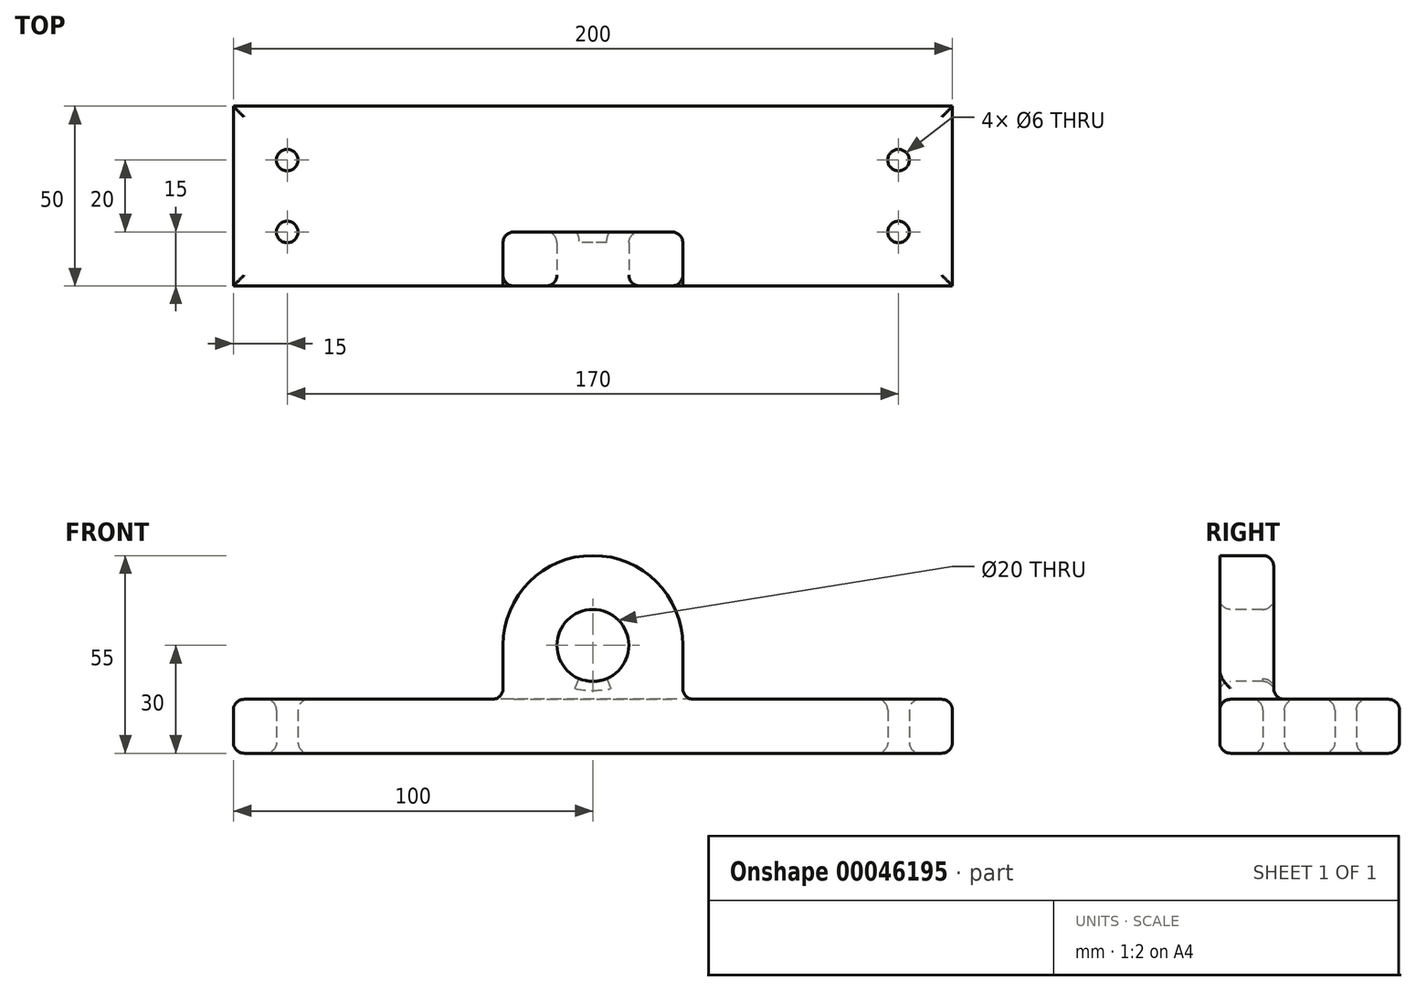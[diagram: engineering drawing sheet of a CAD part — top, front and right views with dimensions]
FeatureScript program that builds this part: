
annotation { "Feature Type Name" : "Feature", "Feature Type Description" : "" }
export const myFeature = defineFeature(function(context is Context, id is Id, definition is map)
    precondition{}
    {
        {
            var Q0;
            Q0=qCreatedBy(makeId("Top.planeOp"),FACE);
            var sketch = newSketch(context, id + "F0", { "sketchPlane" : qUnion([Q0])});
            skLineSegment(sketch, "E0.rect.bottom", {"start": v(100, 25) * mm, "end": v(-100, 25) * mm});
            skLineSegment(sketch, "E0.rect.top", {"start": v(100, -25) * mm, "end": v(-100, -25) * mm});
            skLineSegment(sketch, "E0.rect.left", {"start": v(100, 25) * mm, "end": v(100, -25) * mm});
            skLineSegment(sketch, "E0.rect.right", {"start": v(-100, 25) * mm, "end": v(-100, -25) * mm});
            skPoint(sketch, "E0.rect.middle", {"position": v(0, 0) * mm});
            skLineSegment(sketch, "E1.rect.bottom", {"start": v(85, 10) * mm, "end": v(-85, 10) * mm, "construction": true});
            skLineSegment(sketch, "E1.rect.top", {"start": v(85, -10) * mm, "end": v(-85, -10) * mm, "construction": true});
            skLineSegment(sketch, "E1.rect.left", {"start": v(85, 10) * mm, "end": v(85, -10) * mm, "construction": true});
            skLineSegment(sketch, "E1.rect.right", {"start": v(-85, 10) * mm, "end": v(-85, -10) * mm, "construction": true});
            skCircle(sketch, "E2", {"center": v(-85, 10) * mm, "radius": 3 * mm});
            skCircle(sketch, "E3", {"center": v(85, 10) * mm, "radius": 3 * mm});
            skCircle(sketch, "E4", {"center": v(85, -10) * mm, "radius": 3 * mm});
            skCircle(sketch, "E5", {"center": v(-85, -10) * mm, "radius": 3 * mm});
            skSolve(sketch);
        }
        {
            var Q0;
            Q0=makeQuery(id+"F0.imprint","IMPRINT",FACE,{"disambiguationData":[TD([[makeQuery(id+"F0.imprint","IMPRINT",EDGE,{"derivedFrom":sQuery(id+"F0.wireOp",EDGE,"E0.rect.bottom")}),1.0]])]});
            extrude(context, id + "F1", {"entities" : qUnion([Q0]), "depth" : 15 * mm});
        }
        {
            var Q0;
            Q0=makeQuery(id+"F1.opExtrude","SWEPT_FACE",FACE,{"disambiguationData":[OSD([sQuery(id+"F0.wireOp",EDGE,"E0.rect.top")])]});
            var sketch = newSketch(context, id + "F2", { "sketchPlane" : qUnion([Q0])});
            skLineSegment(sketch, "E6", {"start": v(0, 0) * mm, "end": v(0, 30) * mm, "construction": true});
            skPoint(sketch, "E6.endSnap0", {"position": v(0, 15) * mm});
            skCircle(sketch, "E7", {"center": v(0, 30) * mm, "radius": 25 * mm});
            skLineSegment(sketch, "E8.bottom", {"start": v(-25, 30) * mm, "end": v(25, 30) * mm});
            skLineSegment(sketch, "E8.top", {"start": v(-25, 0) * mm, "end": v(25, 0) * mm});
            skLineSegment(sketch, "E8.left", {"start": v(-25, 30) * mm, "end": v(-25, 0) * mm});
            skLineSegment(sketch, "E8.right", {"start": v(25, 30) * mm, "end": v(25, 0) * mm});
            skCircle(sketch, "E9", {"center": v(0, 30) * mm, "radius": 10 * mm});
            skSolve(sketch);
        }
        {
            var Q0;
            {var subQ0=sQuery(id+"F2.wireOp",EDGE,"E9");var subQ1=sQuery(id+"F2.wireOp",EDGE,"E8.bottom");var subQ3=makeQuery(id+"F2.imprint","INTERSECT",VERTEX,{"disambiguationData":[OD(0.0)],"derivedFrom":[subQ1,subQ0]});Q0=makeQuery(id+"F2.imprint","IMPRINT",FACE,{"disambiguationData":[TD([[makeQuery(id+"F2.imprint","IMPRINT",EDGE,{"disambiguationData":[TD([[subQ3,1.0]])],"derivedFrom":subQ0}),-1.0]])]});}
            var Q1;
            {var subQ0=makeQuery(id+"F1.opExtrude","CAP_EDGE",EDGE,{"disambiguationData":[OSD([sQuery(id+"F0.wireOp",EDGE,"E0.rect.top")])],"isStart":false});var subQ3=sQuery(id+"F2.wireOp",EDGE,"E8.left");var subQ4=makeQuery(id+"F2.imprint","INTERSECT",VERTEX,{"derivedFrom":[subQ0,subQ3]});Q1=makeQuery(id+"F2.imprint","IMPRINT",FACE,{"disambiguationData":[TD([[makeQuery(id+"F2.imprint","IMPRINT",EDGE,{"disambiguationData":[TD([[subQ4,1.0]])],"derivedFrom":subQ0}),-1.0]])]});}
            var Q2;
            {var subQ0=makeQuery(id+"F1.opExtrude","CAP_EDGE",EDGE,{"disambiguationData":[OSD([sQuery(id+"F0.wireOp",EDGE,"E0.rect.top")])],"isStart":false});var subQ3=sQuery(id+"F2.wireOp",EDGE,"E8.right");var subQ4=makeQuery(id+"F2.imprint","INTERSECT",VERTEX,{"derivedFrom":[subQ0,subQ3]});Q2=makeQuery(id+"F2.imprint","IMPRINT",FACE,{"disambiguationData":[TD([[makeQuery(id+"F2.imprint","IMPRINT",EDGE,{"disambiguationData":[TD([[subQ4,-1.0]])],"derivedFrom":subQ0}),-1.0]])]});}
            var Q3;
            {var subQ3=sQuery(id+"F2.wireOp",EDGE,"E8.bottom");var subQ7=sQuery(id+"F2.wireOp",EDGE,"E9");var subQ8=makeQuery(id+"F2.imprint","INTERSECT",VERTEX,{"disambiguationData":[OD(0.0)],"derivedFrom":[subQ3,subQ7]});Q3=makeQuery(id+"F2.imprint","IMPRINT",FACE,{"disambiguationData":[TD([[makeQuery(id+"F2.imprint","IMPRINT",EDGE,{"disambiguationData":[TD([[subQ8,-1.0]])],"derivedFrom":subQ7}),-1.0]])]});}
            var Q4;
            {var subQ10=sQuery(id+"F2.wireOp",EDGE,"E8.top");Q4=makeQuery(id+"F2.imprint","IMPRINT",FACE,{"disambiguationData":[TD([[makeQuery(id+"F2.imprint","IMPRINT",EDGE,{"derivedFrom":subQ10}),-1.0]])]});}
            extrude(context, id + "F3", {"entities" : qUnion([Q0, Q1, Q2, Q3, Q4]), "operationType" : NewBodyOperationType.ADD, "oppositeDirection" : true, "depth" : 15 * mm});
        }
        {
            var Q0;
            Q0=makeQuery(id+"F1.opExtrude","CAP_FACE",FACE,{"disambiguationData":[OSD([sQuery(id+"F0.wireOp",EDGE,"E0.rect.bottom"),sQuery(id+"F0.wireOp",EDGE,"E0.rect.top"),sQuery(id+"F0.wireOp",EDGE,"E0.rect.left"),sQuery(id+"F0.wireOp",EDGE,"E0.rect.right"),sQuery(id+"F0.wireOp",EDGE,"E2"),sQuery(id+"F0.wireOp",EDGE,"E3"),sQuery(id+"F0.wireOp",EDGE,"E4"),sQuery(id+"F0.wireOp",EDGE,"E5")])],"isStart":false});
            var Q1;
            {var subQ0=sQuery(id+"F2.wireOp",EDGE,"E7");var subQ1=sQuery(id+"F2.wireOp",EDGE,"E8.bottom");Q1=makeQuery(id+"F3.opExtrude","CAP_EDGE",EDGE,{"disambiguationData":[OSD([subQ0]),TDD([makeQuery(id+"F2.imprint","IMPRINT",EDGE,{"disambiguationData":[TD([[makeQuery(id+"F2.imprint","INTERSECT",VERTEX,{"derivedFrom":[subQ0,subQ1,sQuery(id+"F2.wireOp",EDGE,"E8.left")]}),1.0]])],"derivedFrom":subQ0})])],"isStart":false});}
            var Q2;
            Q2=makeQuery(id+"F1.opExtrude","CAP_FACE",FACE,{"disambiguationData":[OSD([sQuery(id+"F0.wireOp",EDGE,"E0.rect.bottom"),sQuery(id+"F0.wireOp",EDGE,"E0.rect.top"),sQuery(id+"F0.wireOp",EDGE,"E0.rect.left"),sQuery(id+"F0.wireOp",EDGE,"E0.rect.right"),sQuery(id+"F0.wireOp",EDGE,"E2"),sQuery(id+"F0.wireOp",EDGE,"E3"),sQuery(id+"F0.wireOp",EDGE,"E4"),sQuery(id+"F0.wireOp",EDGE,"E5")])],"isStart":true});
            fillet(context, id + "F4", {"entities" : qUnion([Q0, Q1, Q2]), "radius" : 3 * mm, "tangentPropagation" : true, "allowEdgeOverflow" : false});
        }
        {
            var Q0;
            Q0=makeQuery(id+"F3.opExtrude","CAP_EDGE",EDGE,{"disambiguationData":[OSD([sQuery(id+"F2.wireOp",EDGE,"E9")])],"isStart":true});
            var Q1;
            Q1=makeQuery(id+"F3.opExtrude","CAP_EDGE",EDGE,{"disambiguationData":[OSD([sQuery(id+"F2.wireOp",EDGE,"E9")])],"isStart":false});
            fillet(context, id + "F5", {"entities" : qUnion([Q0, Q1]), "radius" : 3 * mm, "tangentPropagation" : true, "allowEdgeOverflow" : false});
        }
    });
